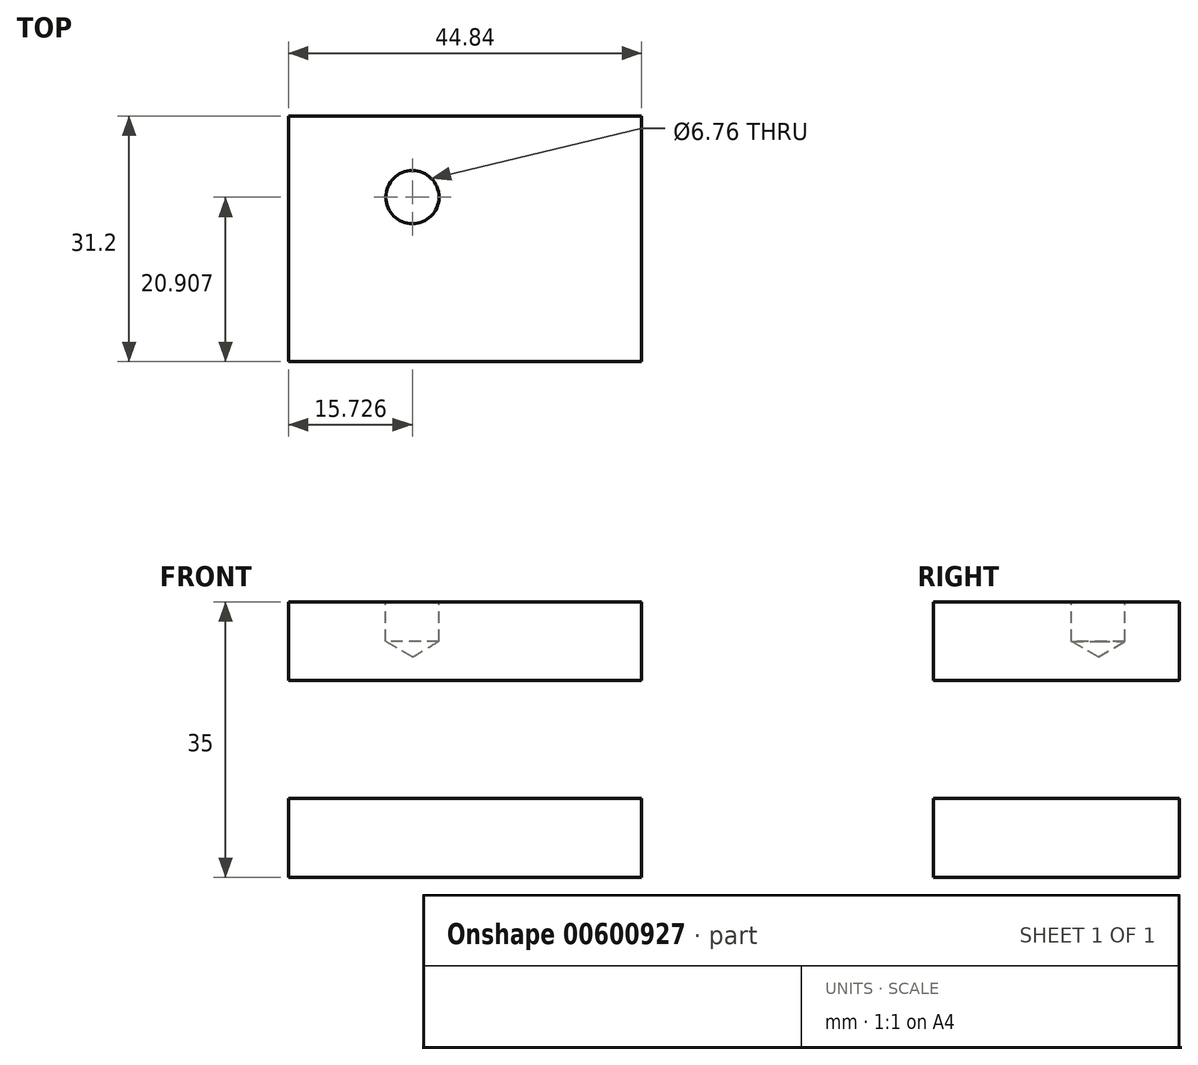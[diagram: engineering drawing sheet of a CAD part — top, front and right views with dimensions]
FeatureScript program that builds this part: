
annotation { "Feature Type Name" : "Feature", "Feature Type Description" : "" }
export const myFeature = defineFeature(function(context is Context, id is Id, definition is map)
    precondition{}
    {
        {
            var Q0;
            Q0=qCreatedBy(makeId("Top.planeOp"),FACE);
            var sketch = newSketch(context, id + "F0", { "sketchPlane" : qUnion([Q0])});
            skLineSegment(sketch, "E0.bottom", {"start": v(-22.42, 15.6) * mm, "end": v(22.42, 15.6) * mm});
            skLineSegment(sketch, "E0.top", {"start": v(-22.42, -15.6) * mm, "end": v(22.42, -15.6) * mm});
            skLineSegment(sketch, "E0.left", {"start": v(-22.42, 15.6) * mm, "end": v(-22.42, -15.6) * mm});
            skLineSegment(sketch, "E0.right", {"start": v(22.42, 15.6) * mm, "end": v(22.42, -15.6) * mm});
            skLineSegment(sketch, "E1", {"start": v(-22.42, -15.6) * mm, "end": v(22.42, 15.6) * mm, "construction": true});
            skSolve(sketch);
        }
        {
            var Q0;
            Q0 = qSketchRegion(id + "F0", true);
            extrude(context, id + "F1", {"entities" : qUnion([Q0]), "depth" : 10 * mm, "offsetDistance" : 25 * mm});
        }
        {
            var Q0;
            Q0=qCreatedBy(makeId("Top.planeOp"),FACE);
            cPlane(context, id + "F2", {"entities" : qUnion([Q0]), "cplaneType" : CPlaneType.OFFSET, "offset" : 25 * mm, "width" : 150 * mm, "height" : 150 * mm});
        }
        {
            var Q0;
            Q0=qCreatedBy(id+"F2.planeOp",FACE);
            var sketch = newSketch(context, id + "F3", { "sketchPlane" : qUnion([Q0])});
            skLineSegment(sketch, "E2.bottom", {"start": v(-22.42, 15.6) * mm, "end": v(22.42, 15.6) * mm});
            skLineSegment(sketch, "E2.top", {"start": v(-22.42, -15.6) * mm, "end": v(22.42, -15.6) * mm});
            skLineSegment(sketch, "E2.left", {"start": v(-22.42, 15.6) * mm, "end": v(-22.42, -15.6) * mm});
            skLineSegment(sketch, "E2.right", {"start": v(22.42, 15.6) * mm, "end": v(22.42, -15.6) * mm});
            skLineSegment(sketch, "E3", {"start": v(-22.42, -15.6) * mm, "end": v(22.42, 15.6) * mm, "construction": true});
            skSolve(sketch);
        }
        {
            var Q0;
            Q0=makeQuery(id+"F3.imprint","IMPRINT",FACE,{"disambiguationData":[TD([[makeQuery(id+"F3.imprint","IMPRINT",EDGE,{"derivedFrom":sQuery(id+"F3.wireOp",EDGE,"E2.bottom")}),-1.0]])]});
            extrude(context, id + "F4", {"entities" : qUnion([Q0]), "depth" : 10 * mm, "offsetDistance" : 25 * mm});
        }
        {
            var Q0;
            Q0=makeQuery(id+"F4.opExtrude","CAP_FACE",FACE,{"disambiguationData":[OSD([sQuery(id+"F3.wireOp",EDGE,"E2.bottom"),sQuery(id+"F3.wireOp",EDGE,"E2.top"),sQuery(id+"F3.wireOp",EDGE,"E2.left"),sQuery(id+"F3.wireOp",EDGE,"E2.right")])],"isStart":false});
            var sketch = newSketch(context, id + "F5", { "sketchPlane" : qUnion([Q0])});
            skPoint(sketch, "E4", {"position": v(-6.7, 5.3) * mm});
            skSolve(sketch);
        }
        {
            var Q0;
            Q0=sQuery(id+"F5.wireOp",VERTEX,"E4");
            var Q1;
            Q1=makeQuery(id+"F4.opExtrude","SWEPT_BODY",BODY,{"disambiguationData":[OSD([sQuery(id+"F3.wireOp",EDGE,"E2.bottom"),sQuery(id+"F3.wireOp",EDGE,"E2.top"),sQuery(id+"F3.wireOp",EDGE,"E2.left"),sQuery(id+"F3.wireOp",EDGE,"E2.right")])]});
            hole(context, id + "F6", {"style" : HoleStyle.SIMPLE, "endStyle" : HoleEndStyle.BLIND, "holeDiameter" : 6.76 * mm, "majorDiameter" : 5 * mm, "holeDepth" : 5 * mm, "isTappedThrough" : true, "tappedDepth" : 12 * mm, "tapClearance" : 3, "startFromSketch" : true, "locations" : qUnion([Q0]), "scope" : qUnion([Q1])});
        }
    });
